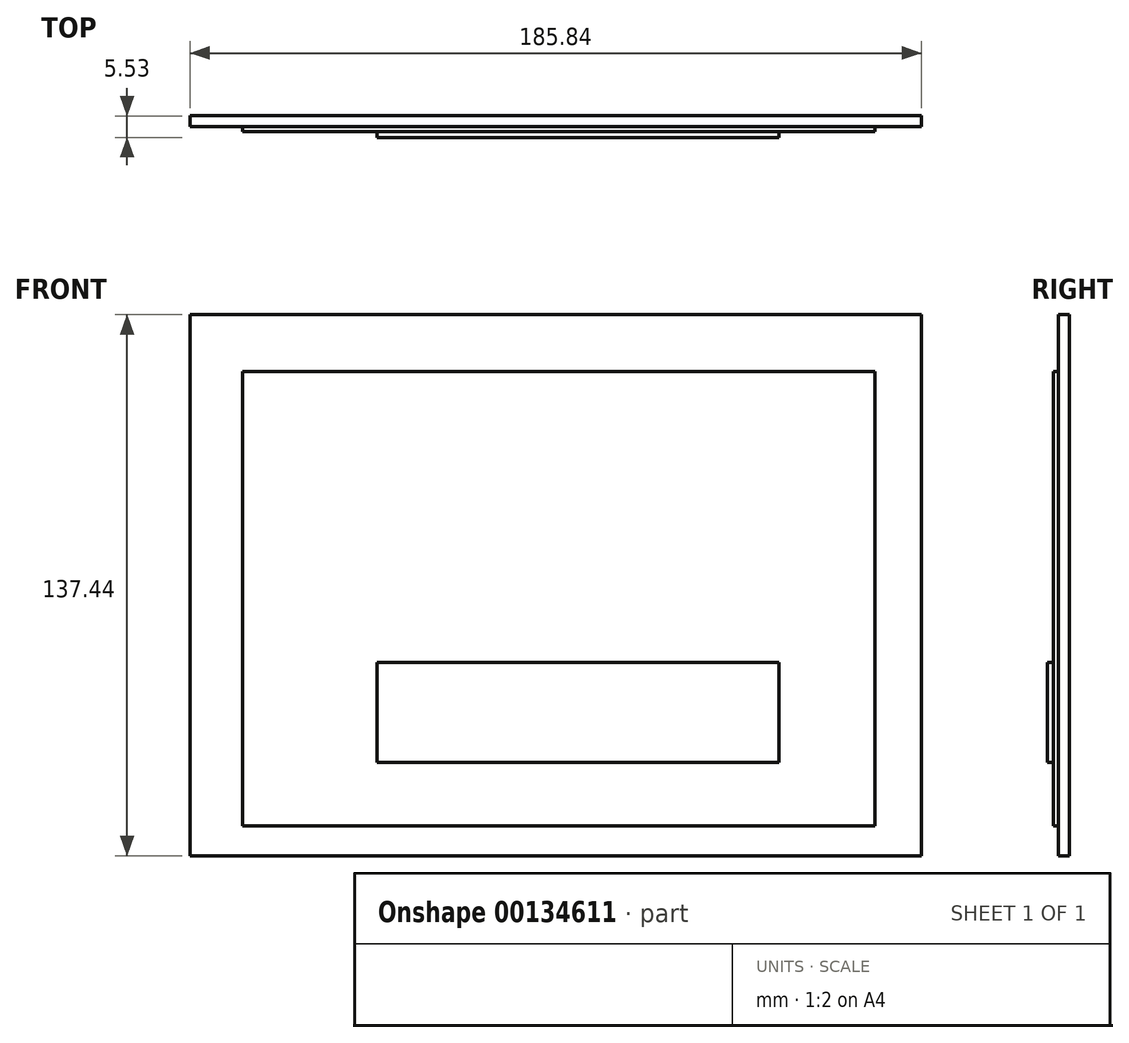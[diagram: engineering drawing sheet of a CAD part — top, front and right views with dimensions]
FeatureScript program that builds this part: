
annotation { "Feature Type Name" : "Feature", "Feature Type Description" : "" }
export const myFeature = defineFeature(function(context is Context, id is Id, definition is map)
    precondition{}
    {
        {
            var Q0;
            Q0=qCreatedBy(makeId("Front.planeOp"),FACE);
            var sketch = newSketch(context, id + "F0", { "sketchPlane" : qUnion([Q0])});
            skLineSegment(sketch, "E0.bottom", {"start": v(-111.58, 63.67) * mm, "end": v(76.16, 63.67) * mm});
            skLineSegment(sketch, "E0.top", {"start": v(-111.58, -75.45) * mm, "end": v(76.16, -75.45) * mm});
            skLineSegment(sketch, "E0.left", {"start": v(-111.58, 63.67) * mm, "end": v(-111.58, -75.45) * mm});
            skLineSegment(sketch, "E0.right", {"start": v(76.16, 63.67) * mm, "end": v(76.16, -75.45) * mm});
            skSolve(sketch);
        }
        {
            var Q0;
            Q0 = qSketchRegion(id + "F0", true);
            var Q1;
            Q1=sQuery(id+"F0.wireOp",EDGE,"E0.right");
            var Q2;
            Q2=sQuery(id+"F0.wireOp",EDGE,"E0.bottom");
            var Q3;
            Q3=sQuery(id+"F0.wireOp",EDGE,"E0.left");
            var Q4;
            Q4=sQuery(id+"F0.wireOp",EDGE,"E0.top");
            extrude(context, id + "F1", {"entities" : qUnion([Q0]), "bodyType" : ToolBodyType.SURFACE, "operationType" : NewBodyOperationType.INTERSECT, "surfaceEntities" : qUnion([Q1, Q2, Q3, Q4]), "endBound" : BoundingType.SYMMETRIC, "depth" : 5.93 * mm});
        }
        {
            var Q0;
            Q0=qCreatedBy(makeId("Front.planeOp"),FACE);
            var sketch = newSketch(context, id + "F2", { "sketchPlane" : qUnion([Q0])});
            skLineSegment(sketch, "E1.bottom", {"start": v(-110.54, 62.85) * mm, "end": v(75.3, 62.85) * mm});
            skLineSegment(sketch, "E1.top", {"start": v(-110.54, -74.6) * mm, "end": v(75.3, -74.6) * mm});
            skLineSegment(sketch, "E1.left", {"start": v(-110.54, 62.85) * mm, "end": v(-110.54, -74.6) * mm});
            skLineSegment(sketch, "E1.right", {"start": v(75.3, 62.85) * mm, "end": v(75.3, -74.6) * mm});
            skSolve(sketch);
        }
        {
            var Q0;
            Q0 = qSketchRegion(id + "F2", true);
            extrude(context, id + "F3", {"entities" : qUnion([Q0]), "oppositeDirection" : true, "depth" : 2.76 * mm});
        }
        {
            var Q0;
            Q0=makeQuery(id+"F3.opExtrude","CAP_FACE",FACE,{"disambiguationData":[OSD([sQuery(id+"F2.wireOp",EDGE,"E1.bottom"),sQuery(id+"F2.wireOp",EDGE,"E1.top"),sQuery(id+"F2.wireOp",EDGE,"E1.left"),sQuery(id+"F2.wireOp",EDGE,"E1.right")])],"isStart":false});
            var sketch = newSketch(context, id + "F4", { "sketchPlane" : qUnion([Q0])});
            skText(sketch, "E2", { "text": "LED", "fontName": "OpenSans-Regular.ttf"});
            const initialGuessF4  = {"E2": [0.05544, 0.03798, 1, 0, 0.0194]};
            skSetInitialGuess(sketch, initialGuessF4);
            skSolve(sketch);
        }
        {
            var Q0;
            Q0=makeQuery(id+"F3.opExtrude","CAP_FACE",FACE,{"disambiguationData":[OSD([sQuery(id+"F2.wireOp",EDGE,"E1.bottom"),sQuery(id+"F2.wireOp",EDGE,"E1.top"),sQuery(id+"F2.wireOp",EDGE,"E1.left"),sQuery(id+"F2.wireOp",EDGE,"E1.right")])],"isStart":true});
            var sketch = newSketch(context, id + "F5", { "sketchPlane" : qUnion([Q0])});
            skLineSegment(sketch, "E3.bottom", {"start": v(-97.24, 48.44) * mm, "end": v(63.4, 48.44) * mm});
            skLineSegment(sketch, "E3.top", {"start": v(-97.24, -67.01) * mm, "end": v(63.4, -67.01) * mm});
            skLineSegment(sketch, "E3.left", {"start": v(-97.24, 48.44) * mm, "end": v(-97.24, -67.01) * mm});
            skLineSegment(sketch, "E3.right", {"start": v(63.4, 48.44) * mm, "end": v(63.4, -67.01) * mm});
            skSolve(sketch);
        }
        {
            var Q0;
            Q0 = qSketchRegion(id + "F5", true);
            extrude(context, id + "F6", {"entities" : qUnion([Q0]), "depth" : 1.25 * mm});
        }
        {
            var Q0;
            Q0=makeQuery(id+"F6.opExtrude","CAP_FACE",FACE,{"disambiguationData":[OSD([sQuery(id+"F5.wireOp",EDGE,"E3.bottom"),sQuery(id+"F5.wireOp",EDGE,"E3.top"),sQuery(id+"F5.wireOp",EDGE,"E3.left"),sQuery(id+"F5.wireOp",EDGE,"E3.right")])],"isStart":false});
            var sketch = newSketch(context, id + "F7", { "sketchPlane" : qUnion([Q0])});
            skLineSegment(sketch, "E4.bottom", {"start": v(-63.01, -25.52) * mm, "end": v(39.04, -25.52) * mm});
            skLineSegment(sketch, "E4.top", {"start": v(-63.01, -50.93) * mm, "end": v(39.04, -50.93) * mm});
            skLineSegment(sketch, "E4.left", {"start": v(-63.01, -25.52) * mm, "end": v(-63.01, -50.93) * mm});
            skLineSegment(sketch, "E4.right", {"start": v(39.04, -25.52) * mm, "end": v(39.04, -50.93) * mm});
            skSolve(sketch);
        }
        {
            var Q0;
            Q0 = qSketchRegion(id + "F7", true);
            extrude(context, id + "F8", {"entities" : qUnion([Q0]), "depth" : 1.52 * mm});
        }
    });
